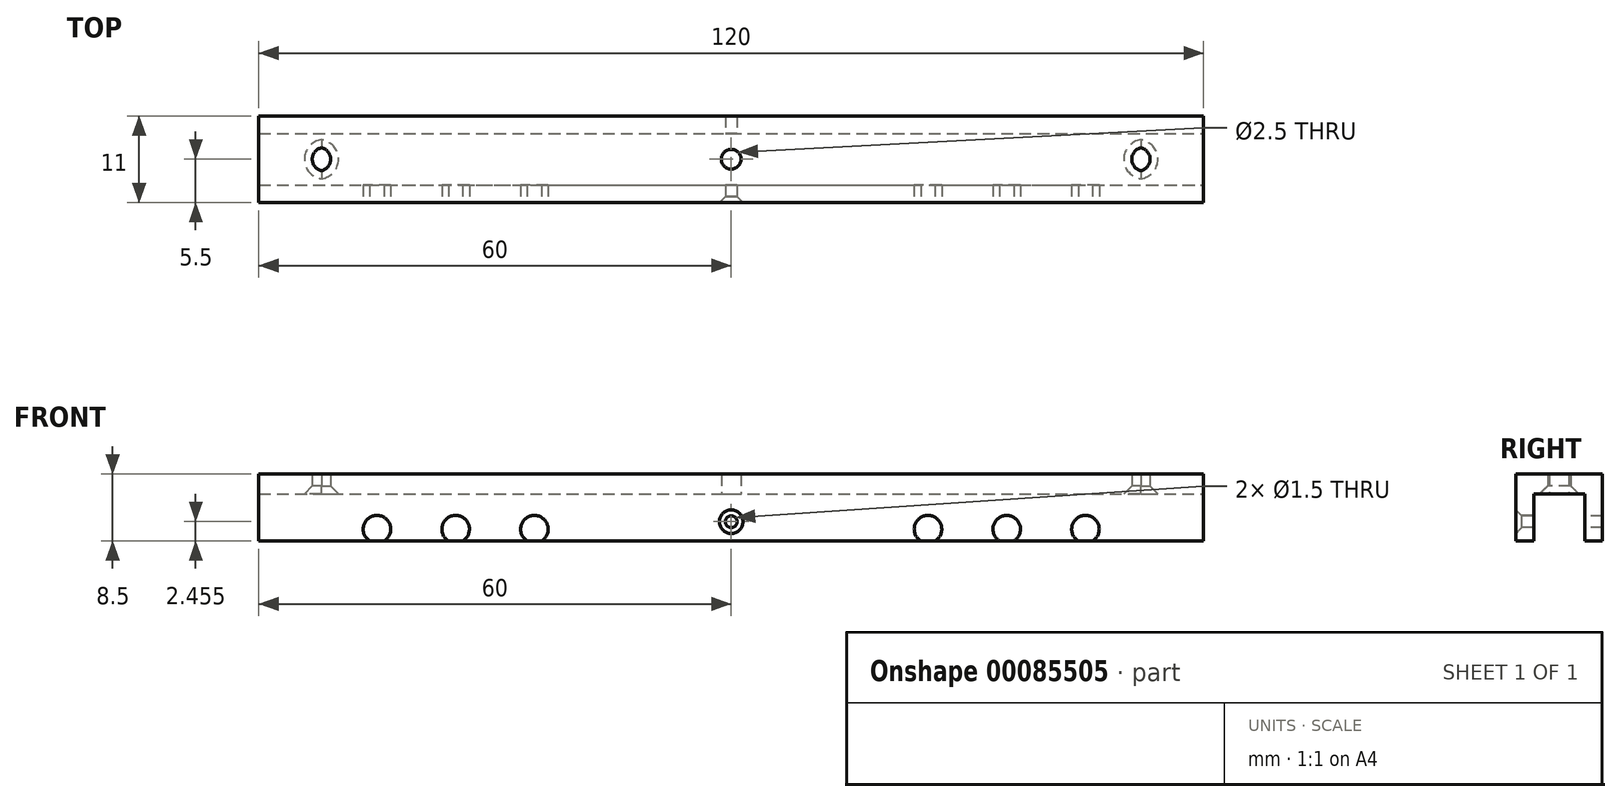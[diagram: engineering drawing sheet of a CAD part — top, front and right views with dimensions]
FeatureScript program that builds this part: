
annotation { "Feature Type Name" : "Feature", "Feature Type Description" : "" }
export const myFeature = defineFeature(function(context is Context, id is Id, definition is map)
    precondition{}
    {
        {
            var Q0;
            Q0=qCreatedBy(makeId("Top.planeOp"),FACE);
            var sketch = newSketch(context, id + "F0", { "sketchPlane" : qUnion([Q0])});
            skLineSegment(sketch, "E0.bottom", {"start": v(-60, 5.5) * mm, "end": v(60, 5.5) * mm});
            skLineSegment(sketch, "E0.top", {"start": v(-60, -5.5) * mm, "end": v(60, -5.5) * mm});
            skLineSegment(sketch, "E0.left", {"start": v(-60, 5.5) * mm, "end": v(-60, -5.5) * mm});
            skLineSegment(sketch, "E0.right", {"start": v(60, 5.5) * mm, "end": v(60, -5.5) * mm});
            skPoint(sketch, "E0.middle", {"position": v(0, 0) * mm});
            skLineSegment(sketch, "E1.bottom", {"start": v(-60, -3.25) * mm, "end": v(60, -3.25) * mm});
            skLineSegment(sketch, "E1.top", {"start": v(-60, 3.25) * mm, "end": v(60, 3.25) * mm});
            skLineSegment(sketch, "E1.left", {"start": v(-60, -3.25) * mm, "end": v(-60, 3.25) * mm});
            skLineSegment(sketch, "E1.right", {"start": v(60, -3.25) * mm, "end": v(60, 3.25) * mm});
            skSolve(sketch);
        }
        {
            var Q0;
            Q0 = qSketchRegion(id + "F0", true);
            extrude(context, id + "F1", {"entities" : qUnion([Q0]), "depth" : 2.5 * mm});
        }
        {
            var Q0;
            {var subQ0=sQuery(id+"F0.wireOp",EDGE,"E0.bottom");Q0=makeQuery(id+"F0.imprint","IMPRINT",FACE,{"disambiguationData":[TD([[makeQuery(id+"F0.imprint","IMPRINT",EDGE,{"derivedFrom":subQ0}),-1.0]])]});}
            var Q1;
            {var subQ0=sQuery(id+"F0.wireOp",EDGE,"E0.top");Q1=makeQuery(id+"F0.imprint","IMPRINT",FACE,{"disambiguationData":[TD([[makeQuery(id+"F0.imprint","IMPRINT",EDGE,{"derivedFrom":subQ0}),1.0]])]});}
            extrude(context, id + "F2", {"entities" : qUnion([Q0, Q1]), "operationType" : NewBodyOperationType.ADD, "oppositeDirection" : true, "depth" : 6 * mm});
        }
        {
            var Q0;
            {var subQ0=sQuery(id+"F0.wireOp",EDGE,"E0.top");Q0=makeQuery(id+"F2.boolean.opBoolean","MERGE",FACE,{"derivedFrom":[makeQuery(id+"F1.opExtrude","SWEPT_FACE",FACE,{"disambiguationData":[OSD([subQ0])]}),makeQuery(id+"F2.opExtrude","SWEPT_FACE",FACE,{"disambiguationData":[OSD([subQ0])]})]});}
            var sketch = newSketch(context, id + "F3", { "sketchPlane" : qUnion([Q0])});
            skLineSegment(sketch, "E2", {"start": v(-60, -4.5) * mm, "end": v(60, -4.5) * mm});
            skPoint(sketch, "E3", {"position": v(-45, -4.5) * mm});
            skPoint(sketch, "E4", {"position": v(-35, -4.5) * mm});
            skPoint(sketch, "E5", {"position": v(-25, -4.5) * mm});
            skPoint(sketch, "E6.MirrorP", {"position": v(45, -4.5) * mm});
            skPoint(sketch, "E7.MirrorP", {"position": v(35, -4.5) * mm});
            skPoint(sketch, "E8.MirrorP", {"position": v(25, -4.5) * mm});
            skSolve(sketch);
        }
        {
            var Q0;
            Q0=makeQuery(id+"F0.imprint","IMPRINT",FACE,{"disambiguationData":[TD([[makeQuery(id+"F0.imprint","IMPRINT",EDGE,{"derivedFrom":sQuery(id+"F0.wireOp",EDGE,"E1.bottom")}),1.0]])]});
            var sketch = newSketch(context, id + "F4", { "sketchPlane" : qUnion([Q0])});
            skSolve(sketch);
        }
        {
            var Q0;
            Q0=makeQuery(id+"F4.imprint","IMPRINT",FACE,{"disambiguationData":[TD([[makeQuery(id+"F4.imprint","IMPRINT",EDGE,{"derivedFrom":makeQuery(id+"F0.imprint","IMPRINT",EDGE,{"derivedFrom":sQuery(id+"F0.wireOp",EDGE,"E1.bottom")})}),1.0]])]});
            var sketch = newSketch(context, id + "F5", { "sketchPlane" : qUnion([Q0])});
            skLineSegment(sketch, "E9", {"start": v(-60.26, 0) * mm, "end": v(60.37, 0) * mm});
            skPoint(sketch, "E10", {"position": v(-52.38, 0) * mm});
            skPoint(sketch, "E11", {"position": v(51.71, 0) * mm});
            skSolve(sketch);
        }
        {
            var Q0;
            Q0=sQuery(id+"F5.wireOp",VERTEX,"E10");
            var Q1;
            Q1=sQuery(id+"F5.wireOp",VERTEX,"E11");
            var Q2;
            Q2=makeQuery(id+"F1.opExtrude","SWEPT_BODY",BODY,{"disambiguationData":[OSD([sQuery(id+"F0.wireOp",EDGE,"E0.bottom"),sQuery(id+"F0.wireOp",EDGE,"E0.top"),sQuery(id+"F0.wireOp",EDGE,"E0.left"),sQuery(id+"F0.wireOp",EDGE,"E0.right"),sQuery(id+"F0.wireOp",EDGE,"E1.left"),sQuery(id+"F0.wireOp",EDGE,"E1.right")])]});
            hole(context, id + "F6", {"style" : HoleStyle.C_SINK, "endStyle" : HoleEndStyle.THROUGH, "oppositeDirection" : true, "holeDiameter" : 3 * mm, "cSinkDiameter" : 5 * mm, "cSinkAngle" : 90 * degree, "locations" : qUnion([Q0, Q1]), "scope" : qUnion([Q2]), "isTappedThrough" : true});
        }
        {
            var Q0;
            Q0=sQuery(id+"F0.wireOp",VERTEX,"E0.middle");
            var Q1;
            Q1=makeQuery(id+"F1.opExtrude","SWEPT_BODY",BODY,{"disambiguationData":[OSD([sQuery(id+"F0.wireOp",EDGE,"E0.bottom"),sQuery(id+"F0.wireOp",EDGE,"E0.top"),sQuery(id+"F0.wireOp",EDGE,"E0.left"),sQuery(id+"F0.wireOp",EDGE,"E0.right"),sQuery(id+"F0.wireOp",EDGE,"E1.left"),sQuery(id+"F0.wireOp",EDGE,"E1.right")])]});
            hole(context, id + "F7", {"style" : HoleStyle.SIMPLE, "endStyle" : HoleEndStyle.THROUGH, "oppositeDirection" : true, "holeDiameter" : 2.5 * mm, "startFromSketch" : true, "locations" : qUnion([Q0]), "scope" : qUnion([Q1]), "isTappedThrough" : true});
        }
        {
            var Q0;
            Q0=sQuery(id+"F3.wireOp",VERTEX,"E3");
            var Q1;
            Q1=sQuery(id+"F3.wireOp",VERTEX,"E4");
            var Q2;
            Q2=sQuery(id+"F3.wireOp",VERTEX,"E5");
            var Q3;
            Q3=sQuery(id+"F3.wireOp",VERTEX,"eeeb7a01-0845-4edd-9b9a-a68d3a98e50b");
            var Q4;
            Q4=sQuery(id+"F3.wireOp",VERTEX,"72c2a17d-0be0-4e80-9c15-4712fa0b8d99");
            var Q5;
            Q5=sQuery(id+"F3.wireOp",VERTEX,"289c1686-2a6c-4b9f-a52b-3f8fbe5a3a24");
            var Q6;
            Q6=sQuery(id+"F3.wireOp",VERTEX,"E8.MirrorP");
            var Q7;
            Q7=sQuery(id+"F3.wireOp",VERTEX,"E7.MirrorP");
            var Q8;
            Q8=sQuery(id+"F3.wireOp",VERTEX,"E6.MirrorP");
            var Q9;
            Q9=makeQuery(id+"F1.opExtrude","SWEPT_BODY",BODY,{"disambiguationData":[OSD([sQuery(id+"F0.wireOp",EDGE,"E0.bottom"),sQuery(id+"F0.wireOp",EDGE,"E0.top"),sQuery(id+"F0.wireOp",EDGE,"E0.left"),sQuery(id+"F0.wireOp",EDGE,"E0.right"),sQuery(id+"F0.wireOp",EDGE,"E1.left"),sQuery(id+"F0.wireOp",EDGE,"E1.right")])]});
            hole(context, id + "F8", {"style" : HoleStyle.SIMPLE, "endStyle" : HoleEndStyle.BLIND, "holeDiameter" : 3.5 * mm, "holeDepth" : 3 * mm, "locations" : qUnion([Q0, Q1, Q2, Q3, Q4, Q5, Q6, Q7, Q8]), "scope" : qUnion([Q9])});
        }
        {
            var Q0;
            {var subQ0=sQuery(id+"F3.wireOp",EDGE,"E2");Q0=makeQuery(id+"F3.imprint","IMPRINT",FACE,{"disambiguationData":[TD([[makeQuery(id+"F3.imprint","IMPRINT",EDGE,{"derivedFrom":subQ0}),1.0]])]});}
            var sketch = newSketch(context, id + "F9", { "sketchPlane" : qUnion([Q0])});
            skPoint(sketch, "E12", {"position": v(0, -3.54) * mm});
            skSolve(sketch);
        }
        {
            var Q0;
            Q0=sQuery(id+"F9.wireOp",VERTEX,"E12");
            var Q1;
            Q1=makeQuery(id+"F1.opExtrude","SWEPT_BODY",BODY,{"disambiguationData":[OSD([sQuery(id+"F0.wireOp",EDGE,"E0.bottom"),sQuery(id+"F0.wireOp",EDGE,"E0.top"),sQuery(id+"F0.wireOp",EDGE,"E0.left"),sQuery(id+"F0.wireOp",EDGE,"E0.right"),sQuery(id+"F0.wireOp",EDGE,"E1.left"),sQuery(id+"F0.wireOp",EDGE,"E1.right")])]});
            hole(context, id + "F10", {"style" : HoleStyle.C_SINK, "endStyle" : HoleEndStyle.THROUGH, "holeDiameter" : 1.5 * mm, "cSinkDiameter" : 3 * mm, "cSinkAngle" : 90 * degree, "locations" : qUnion([Q0]), "scope" : qUnion([Q1]), "isTappedThrough" : true});
        }
        {
            var Q0;
            Q0=makeQuery(id+"F1.opExtrude","SWEPT_BODY",BODY,{"disambiguationData":[OSD([sQuery(id+"F0.wireOp",EDGE,"E0.bottom"),sQuery(id+"F0.wireOp",EDGE,"E0.top"),sQuery(id+"F0.wireOp",EDGE,"E0.left"),sQuery(id+"F0.wireOp",EDGE,"E0.right"),sQuery(id+"F0.wireOp",EDGE,"E1.left"),sQuery(id+"F0.wireOp",EDGE,"E1.right")])]});
            var Q1;
            Q1=qCreatedBy(makeId("Right.planeOp"),FACE);
            mirror(context, id + "F11", {"operationType" : NewBodyOperationType.ADD, "entities" : qUnion([Q0]), "mirrorPlane" : qUnion([Q1])});
        }
    });
